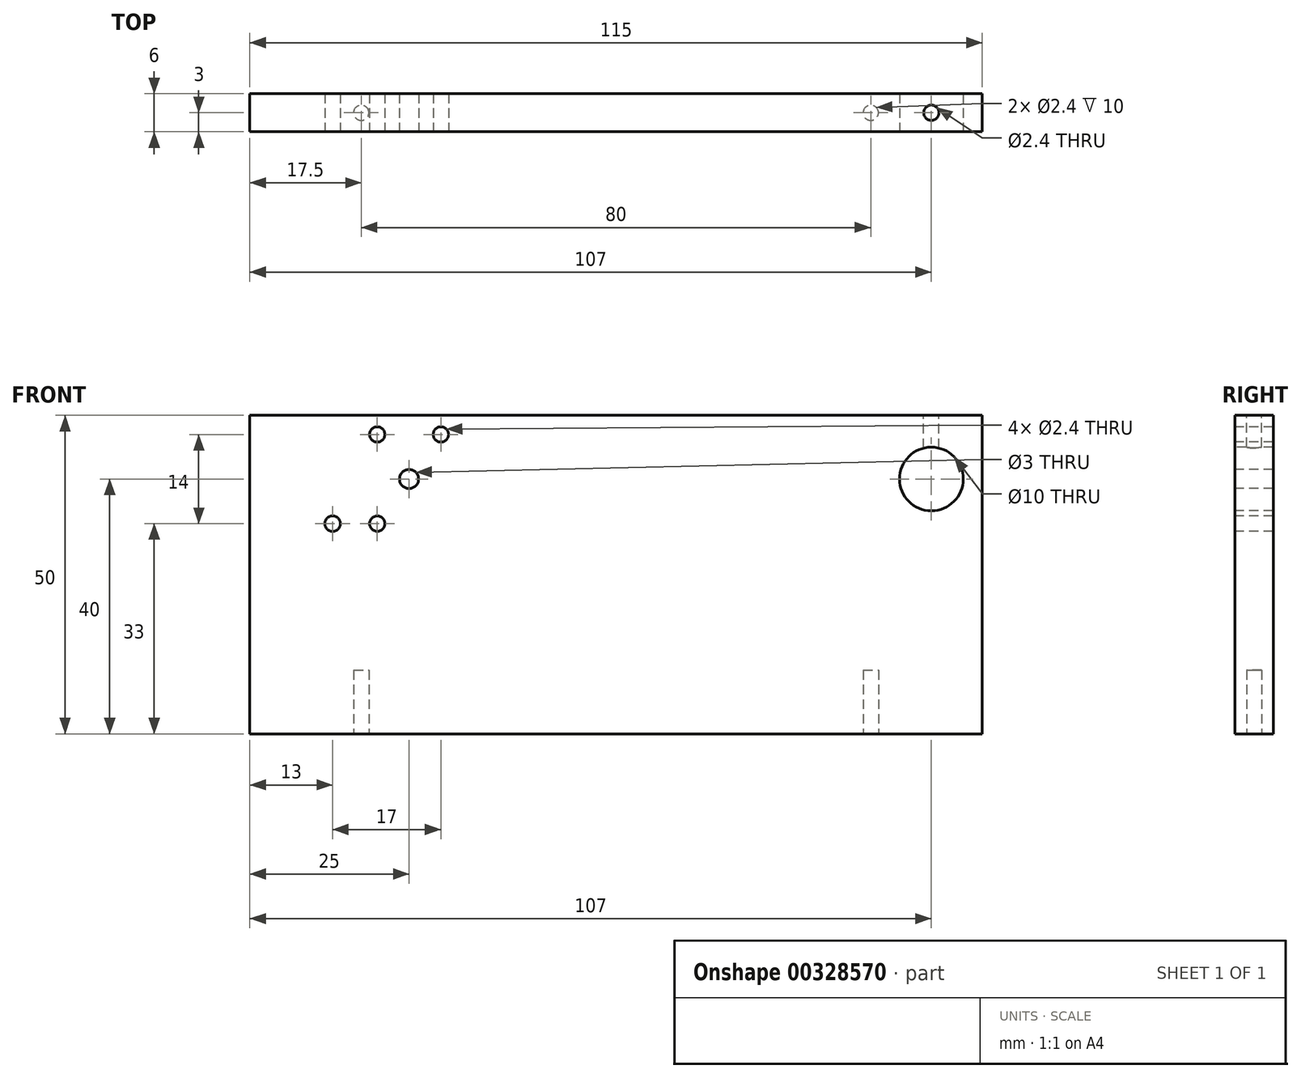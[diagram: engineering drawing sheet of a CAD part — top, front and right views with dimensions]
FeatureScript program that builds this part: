
annotation { "Feature Type Name" : "Feature", "Feature Type Description" : "" }
export const myFeature = defineFeature(function(context is Context, id is Id, definition is map)
    precondition{}
    {
        {
            var Q0;
            Q0=qCreatedBy(makeId("Front.planeOp"),FACE);
            var sketch = newSketch(context, id + "F0", { "sketchPlane" : qUnion([Q0])});
            skLineSegment(sketch, "E0.bottom", {"start": v(57.5, 25) * mm, "end": v(-57.5, 25) * mm});
            skLineSegment(sketch, "E0.top", {"start": v(57.5, -25) * mm, "end": v(-57.5, -25) * mm});
            skLineSegment(sketch, "E0.left", {"start": v(57.5, 25) * mm, "end": v(57.5, -25) * mm});
            skLineSegment(sketch, "E0.right", {"start": v(-57.5, 25) * mm, "end": v(-57.5, -25) * mm});
            skPoint(sketch, "E0.middle", {"position": v(0, 0) * mm});
            skSolve(sketch);
        }
        {
            var Q0;
            Q0 = qSketchRegion(id + "F0", true);
            extrude(context, id + "F1", {"entities" : qUnion([Q0]), "depth" : 3 * mm, "hasSecondDirection" : true, "secondDirectionOppositeDirection" : true, "secondDirectionDepth" : 3 * mm});
        }
        {
            var Q0;
            Q0=makeQuery(id+"F1.opExtrude","CAP_FACE",FACE,{"disambiguationData":[OSD([sQuery(id+"F0.wireOp",EDGE,"E0.bottom"),sQuery(id+"F0.wireOp",EDGE,"E0.top"),sQuery(id+"F0.wireOp",EDGE,"E0.left"),sQuery(id+"F0.wireOp",EDGE,"E0.right")])],"isStart":false});
            var sketch = newSketch(context, id + "F2", { "sketchPlane" : qUnion([Q0])});
            skCircle(sketch, "E1", {"center": v(49.5, 15) * mm, "radius": 5 * mm});
            skCircle(sketch, "E2", {"center": v(-37.5, 22) * mm, "radius": 1.2 * mm});
            skCircle(sketch, "E3", {"center": v(-27.5, 22) * mm, "radius": 1.2 * mm});
            skCircle(sketch, "E4", {"center": v(-32.5, 15) * mm, "radius": 1.5 * mm});
            skCircle(sketch, "E5", {"center": v(-37.5, 8) * mm, "radius": 1.2 * mm});
            skCircle(sketch, "E6", {"center": v(-44.5, 8) * mm, "radius": 1.2 * mm});
            skSolve(sketch);
        }
        {
            var Q0;
            Q0 = qSketchRegion(id + "F2", true);
            extrude(context, id + "F3", {"entities" : qUnion([Q0]), "operationType" : NewBodyOperationType.REMOVE, "endBound" : BoundingType.THROUGH_ALL, "oppositeDirection" : true, "depth" : 25 * mm});
        }
        {
            var Q0;
            Q0=makeQuery(id+"F1.opExtrude","SWEPT_FACE",FACE,{"disambiguationData":[OSD([sQuery(id+"F0.wireOp",EDGE,"E0.bottom")])]});
            var sketch = newSketch(context, id + "F4", { "sketchPlane" : qUnion([Q0])});
            skCircle(sketch, "E7", {"center": v(49.5, 0) * mm, "radius": 1.2 * mm});
            skSolve(sketch);
        }
        {
            var Q0;
            Q0 = qSketchRegion(id + "F4", true);
            extrude(context, id + "F5", {"entities" : qUnion([Q0]), "operationType" : NewBodyOperationType.REMOVE, "endBound" : BoundingType.UP_TO_NEXT, "oppositeDirection" : true, "depth" : 25 * mm});
        }
        {
            var Q0;
            Q0=makeQuery(id+"F1.opExtrude","SWEPT_FACE",FACE,{"disambiguationData":[OSD([sQuery(id+"F0.wireOp",EDGE,"E0.top")])]});
            var sketch = newSketch(context, id + "F6", { "sketchPlane" : qUnion([Q0])});
            skCircle(sketch, "E8", {"center": v(-40, 0) * mm, "radius": 1.2 * mm});
            skCircle(sketch, "E9", {"center": v(40, 0) * mm, "radius": 1.2 * mm});
            skSolve(sketch);
        }
        {
            var Q0;
            Q0 = qSketchRegion(id + "F6", true);
            extrude(context, id + "F7", {"entities" : qUnion([Q0]), "operationType" : NewBodyOperationType.REMOVE, "oppositeDirection" : true, "depth" : 10 * mm});
        }
    });
